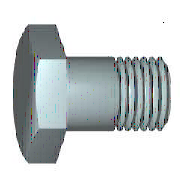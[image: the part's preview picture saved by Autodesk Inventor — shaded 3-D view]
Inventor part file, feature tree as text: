
AUTODESK INVENTOR PART (.ipt)
format: ipt  version: 2016 (Build 200138000, 138)  size: 187,904 bytes
history: native  units: mm (DEFAULTED — no unit token found)
features: sketch x3, extrude x1, chamfer x1, plane x1
ambient origin geometry x7: Origin, YZ Plane, XZ Plane, X Axis, Y Axis, Z Axis, Center Point
bodies: Solid1 (feature_tree), Body (feature_tree)
feature tree (6):
  extrude  "Head"  Depth=30.0mm
  chamfer  "Chamfer1"  Distance=6.9mm
  plane  "Work Plane1"
  sketch  "Sketch1"  dims[d0=100.0mm d1=30.0mm]
  sketch  "Sketch2"  dims[d2=12.0mm]
  sketch  "Sketch4"  dims[d12=90.0deg d3=6.9mm d4=0.0mm d5=30.0deg d21=90.0deg d6=1.073538mm d7=1.073638mm d8=0.0mm d9=0.6001mm d10=17.4mm d11=19.0mm d13=1.073638mm d14=12.0mm d15=30.0mm d16=0.0mm d19=19.0mm d55=45.0deg d57=0.0mm d58=0.0mm]
